# Revit family: Пергола «Радуга» Арт 12273
name_source: partatom
category: Антураж
revit_build: Autodesk Revit 2018 (Build: 20180423_1000(x64)
units: mm (PartAtom-declared; Revit-internal decimal feet)

## family parameters
Всегда вертикально = Да
Источник визуального образа = Геометрия семейства
На основе рабочей плоскости = Нет
Общий = Нет
При загрузке вырезать с полостями = Нет
Точка расчета площади = Нет

## types (3) — shared parameters
URL = https://hobbyka.ru
Артикул товара = Арт. 12273
Высота = 3000 мм
Группа модели = Навесы, перголы и ротонды
Изготовитель = ООО «Хоббика»
Кол-во реек = 20
Материал изделия = Сталь, дерево
Предупреждение = Нет
Цвет навеса = Дерево
Цвет опор = Сталь
Ширина = 3000 мм

## per-type parameters (varying)
| type | Длина | Заказная длина | Изображение типоразмера | Лавка | Описание | Поликарбонат | Рейка |
| Пергола «Радуга». Версия с лавочкой | 2990 мм | 2990 мм | Пергола «Радуга» Арт 12273 с лавкой.jpg | Да | Пергола «Радуга». Версия с лавочкой | Нет | Да |
| Пергола «Радуга». Версия без лавочки | 3000 мм | 3000 мм | Пергола «Радуга» Арт 12273 без лавки.jpg | Нет | Пергола «Радуга». Версия без лавочки | Нет | Да |
| Пергола «Радуга». Версия с поликарбонатной крышей | 2990 мм | 2990 мм | Пергола «Радуга» Арт 12273 с лавкой.jpg | Нет | Пергола «Радуга». Версия с поликарбонатной крышей без лавки | Да | Нет |
